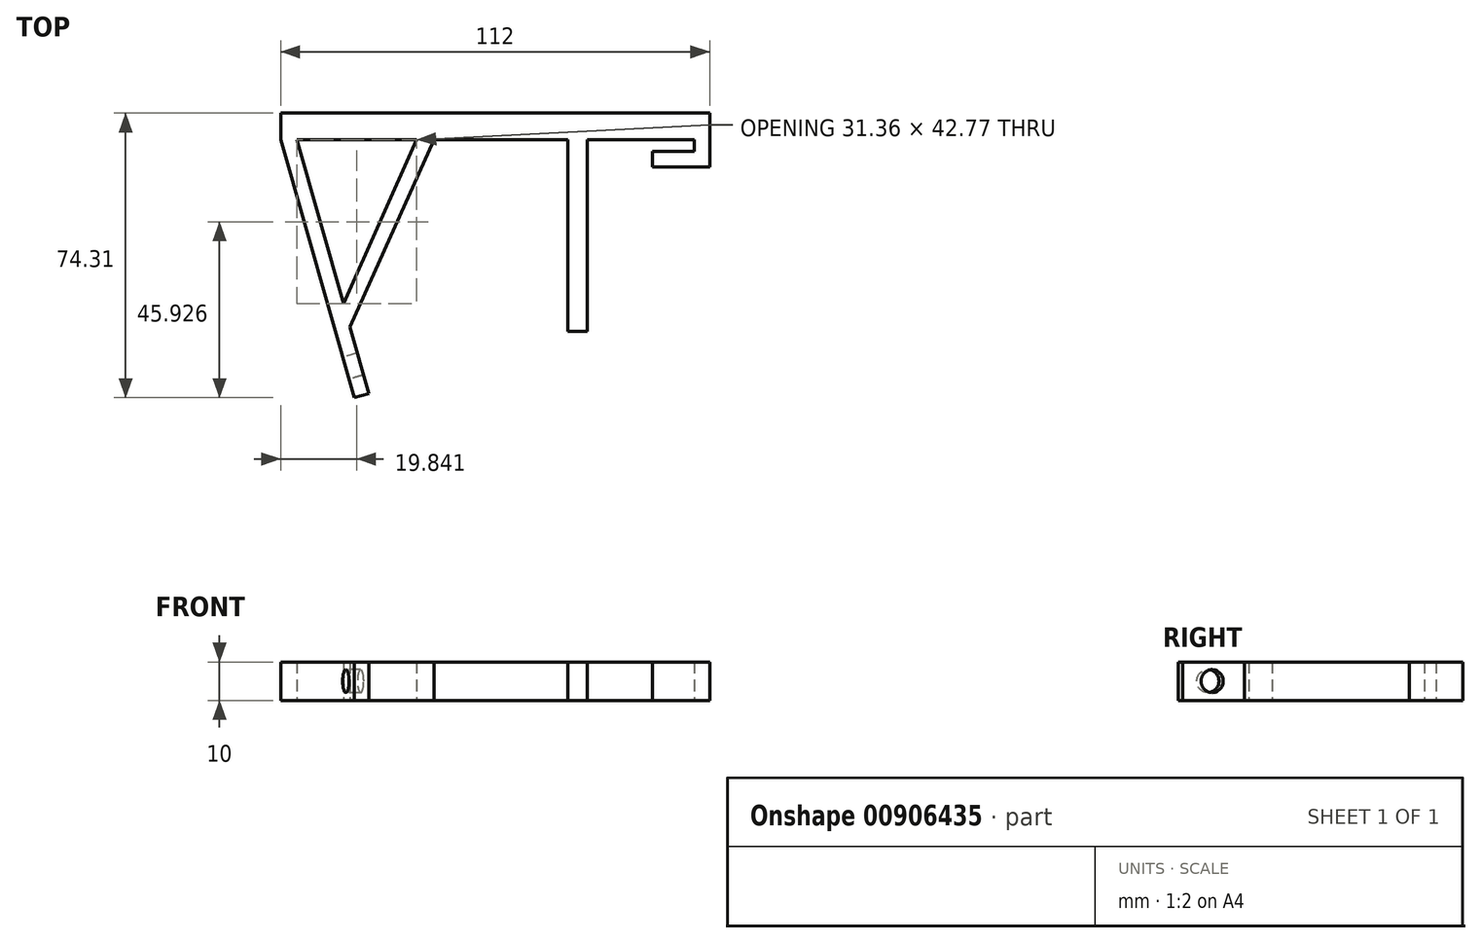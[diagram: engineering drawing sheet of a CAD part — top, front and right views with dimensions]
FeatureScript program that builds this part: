
annotation { "Feature Type Name" : "Feature", "Feature Type Description" : "" }
export const myFeature = defineFeature(function(context is Context, id is Id, definition is map)
    precondition{}
    {
        {
            var Q0;
            Q0=qCreatedBy(makeId("Top.planeOp"),FACE);
            var sketch = newSketch(context, id + "F0", { "sketchPlane" : qUnion([Q0])});
            skLineSegment(sketch, "E0.bottom", {"start": v(0, 0) * mm, "end": v(-80, 0) * mm});
            skLineSegment(sketch, "E0.top", {"start": v(0, 7) * mm, "end": v(-80, 7) * mm});
            skLineSegment(sketch, "E0.left", {"start": v(0, 0) * mm, "end": v(0, 7) * mm});
            skLineSegment(sketch, "E0.right", {"start": v(-80, 0) * mm, "end": v(-80, 7) * mm});
            skLineSegment(sketch, "E1.bottom", {"start": v(0, 0) * mm, "end": v(-5, 0) * mm});
            skLineSegment(sketch, "E1.top", {"start": v(0, -50) * mm, "end": v(-5, -50) * mm});
            skLineSegment(sketch, "E1.left", {"start": v(0, 0) * mm, "end": v(0, -50) * mm});
            skLineSegment(sketch, "E1.right", {"start": v(-5, 0) * mm, "end": v(-5, -50) * mm});
            skLineSegment(sketch, "E2", {"start": v(-80, 0) * mm, "end": v(-60.77, -67.3) * mm});
            skLineSegment(sketch, "E3", {"start": v(-60.77, -67.3) * mm, "end": v(-56.92, -66.2) * mm});
            skLineSegment(sketch, "E4", {"start": v(-56.92, -66.2) * mm, "end": v(-75.84, 0) * mm});
            skLineSegment(sketch, "E5.bottom", {"start": v(0, 0) * mm, "end": v(0, 0) * mm});
            skLineSegment(sketch, "E5.top", {"start": v(0, 7) * mm, "end": v(0, 7) * mm});
            skLineSegment(sketch, "E6.bottom", {"start": v(0, 7) * mm, "end": v(32, 7) * mm});
            skLineSegment(sketch, "E6.top", {"start": v(0, 0) * mm, "end": v(32, 0) * mm});
            skLineSegment(sketch, "E6.left", {"start": v(0, 7) * mm, "end": v(0, 0) * mm});
            skLineSegment(sketch, "E6.right", {"start": v(32, 7) * mm, "end": v(32, 0) * mm});
            skLineSegment(sketch, "E7.bottom", {"start": v(32, 0) * mm, "end": v(28, 0) * mm});
            skLineSegment(sketch, "E7.top", {"start": v(32, -3) * mm, "end": v(28, -3) * mm});
            skLineSegment(sketch, "E7.left", {"start": v(32, 0) * mm, "end": v(32, -3) * mm});
            skLineSegment(sketch, "E7.right", {"start": v(28, 0) * mm, "end": v(28, -3) * mm});
            skLineSegment(sketch, "E8.bottom", {"start": v(32, -3) * mm, "end": v(17, -3) * mm});
            skLineSegment(sketch, "E8.top", {"start": v(32, -7) * mm, "end": v(17, -7) * mm});
            skLineSegment(sketch, "E8.left", {"start": v(32, -3) * mm, "end": v(32, -7) * mm});
            skLineSegment(sketch, "E8.right", {"start": v(17, -3) * mm, "end": v(17, -7) * mm});
            skLineSegment(sketch, "E9", {"start": v(-44.48, 0) * mm, "end": v(-63.62, -42.77) * mm});
            skLineSegment(sketch, "E10", {"start": v(-63.62, -42.77) * mm, "end": v(-61.87, -48.87) * mm});
            skLineSegment(sketch, "E11", {"start": v(-61.87, -48.87) * mm, "end": v(-40, 0) * mm});
            skLineSegment(sketch, "E12", {"start": v(-40, 0) * mm, "end": v(-44.48, 0) * mm});
            skSolve(sketch);
        }
        {
            var Q0;
            Q0=qSketchRegion(id+"F0",true);
            extrude(context, id + "F1", {"entities" : qUnion([Q0]), "depth" : 10 * mm, "offsetDistance" : 25 * mm});
        }
        {
            var Q0;
            Q0=makeQuery(id+"F1.opExtrude","SWEPT_FACE",FACE,{"disambiguationData":[OSD([sQuery(id+"F0.wireOp",EDGE,"E2")])]});
            var sketch = newSketch(context, id + "F2", { "sketchPlane" : qUnion([Q0])});
            skLineSegment(sketch, "E13", {"start": v(48.02, 0) * mm, "end": v(38.02, 0) * mm});
            skLineSegment(sketch, "E14", {"start": v(38.02, 0) * mm, "end": v(38.02, 5) * mm});
            skSolve(sketch);
        }
        {
            var Q0;
            {var subQ3=sQuery(id+"F2.wireOp",EDGE,"E13");Q0=makeQuery(id+"F2.imprint","IMPRINT",FACE,{"disambiguationData":[TD([[makeQuery(id+"F2.imprint","IMPRINT",EDGE,{"derivedFrom":subQ3}),1.0]])]});}
            var sketch = newSketch(context, id + "F3", { "sketchPlane" : qUnion([Q0])});
            skCircle(sketch, "E15", {"center": v(39.96, 5.03) * mm, "radius": 3 * mm});
            skSolve(sketch);
        }
        {
            var Q0;
            Q0=qSketchRegion(id+"F3",true);
            extrude(context, id + "F4", {"entities" : qUnion([Q0]), "operationType" : NewBodyOperationType.REMOVE, "oppositeDirection" : true, "depth" : 10 * mm, "offsetDistance" : 25 * mm});
        }
    });
